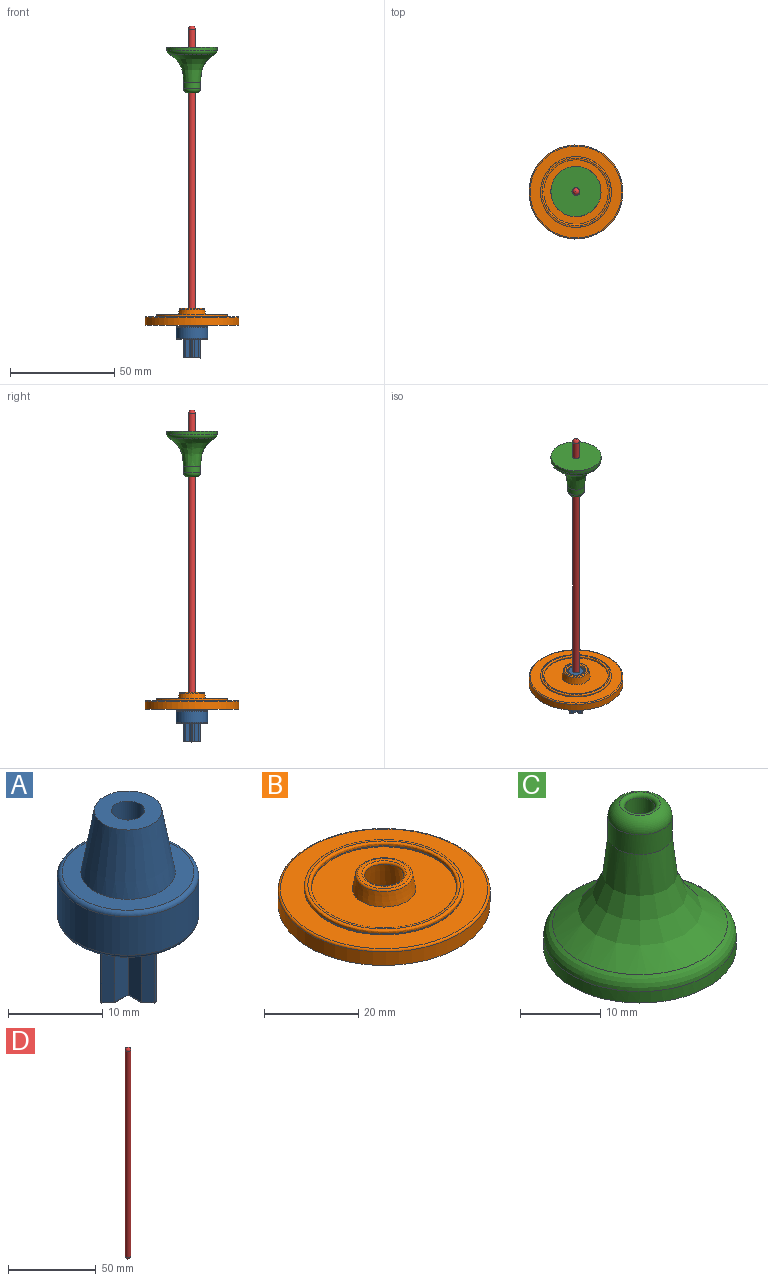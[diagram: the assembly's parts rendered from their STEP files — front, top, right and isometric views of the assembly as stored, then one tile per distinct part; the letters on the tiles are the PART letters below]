
ASSEMBLY  parts=4 mates=4
PART A: 51 faces, bbox 16.2x16.2x23 mm
  f0: cylinder r=7.5mm len=15mm, axis (0,0,-1), area 235.6mm2, adj f49,f50
  f1: plane 14x14mm, normal (0,0,1), area 75.4mm2, adj f44,f50
  f2: plane 14x14mm, normal (0,0,-1), area 126.7mm2, adj f3,f4,f5,f6,f7,f8,f9,f10
  f3: plane 8.8x2mm, normal (-1,0,0), area 17.6mm2, adj f2,f4,f18,f38
  f4: plane 8.8x2mm, normal (0,-1,0), area 17.6mm2, adj f2,f3,f13,f41
  f5: plane 8.8x2mm, normal (0,1,0), area 17.6mm2, adj f2,f6,f12,f37
  f6: plane 8.8x2mm, normal (-1,0,0), area 17.6mm2, adj f2,f5,f15,f35
  f7: plane 8.8x2mm, normal (1,0,0), area 17.6mm2, adj f2,f8,f14,f25
  f8: plane 8.8x2mm, normal (0,1,0), area 17.6mm2, adj f2,f7,f17,f23
  f9: plane 8.8x2mm, normal (0,-1,0), area 17.6mm2, adj f2,f10,f16,f26
  f10: plane 8.8x2mm, normal (1,0,0), area 17.6mm2, adj f2,f9,f19,f29
  f11: plane 7.83x7.83mm, normal (0,0,-1), area 21.7mm2, adj f21,f23,f24,f25,f26,f27,f29,f32
  f12: plane 8.8x0.96mm, normal (-0.71,0.71,0), area 11.9mm2, adj f2,f5,f39,f40
  f13: plane 8.8x0.96mm, normal (-0.71,-0.71,0), area 11.9mm2, adj f2,f4,f40,f43
  f14: plane 8.8x0.96mm, normal (0.71,0.71,0), area 11.9mm2, adj f2,f7,f27,f28
  f15: plane 8.8x0.96mm, normal (-0.71,0.71,0), area 11.9mm2, adj f2,f6,f28,f33
  f16: plane 8.8x0.96mm, normal (0.71,-0.71,0), area 11.9mm2, adj f2,f9,f20,f24
  f17: plane 8.8x0.96mm, normal (0.71,0.71,0), area 11.9mm2, adj f2,f8,f20,f21
  f18: plane 8.8x0.96mm, normal (-0.71,-0.71,0), area 11.9mm2, adj f2,f3,f31,f36
  f19: plane 8.8x0.96mm, normal (0.71,-0.71,0), area 11.9mm2, adj f2,f10,f31,f32
  f20: cylinder r=0.2mm len=8.8mm, axis (0,0,-1), area 2.8mm2, adj f2,f16,f17,f22
  f21: cylinder r=0.2mm len=1.1mm, axis (-0.71,0.71,0), area 0.4mm2, adj f11,f17,f22,f23
  f22: sphere r=0.2mm, area 0.1mm2, adj f20,f21,f24
  f23: cylinder r=0.2mm len=2.2mm, axis (-1,0,0), area 0.6mm2, adj f8,f11,f21,f25
  f24: cylinder r=0.2mm len=1.1mm, axis (0.71,0.71,0), area 0.4mm2, adj f11,f16,f22,f26
  f25: cylinder r=0.2mm len=2.2mm, axis (0,1,0), area 0.6mm2, adj f7,f11,f23,f27
  f26: cylinder r=0.2mm len=2.2mm, axis (1,0,0), area 0.6mm2, adj f9,f11,f24,f29
  f27: cylinder r=0.2mm len=1.1mm, axis (-0.71,0.71,0), area 0.4mm2, adj f11,f14,f25,f30
  f28: cylinder r=0.2mm len=8.8mm, axis (0,0,-1), area 2.8mm2, adj f2,f14,f15,f30
  f29: cylinder r=0.2mm len=2.2mm, axis (0,1,0), area 0.6mm2, adj f10,f11,f26,f32
  f30: sphere r=0.2mm, area 0.1mm2, adj f27,f28,f33
  f31: cylinder r=0.2mm len=8.8mm, axis (0,0,-1), area 2.8mm2, adj f2,f18,f19,f34
  f32: cylinder r=0.2mm len=1.1mm, axis (0.71,0.71,0), area 0.4mm2, adj f11,f19,f29,f34
  f33: cylinder r=0.2mm len=1.1mm, axis (-0.71,-0.71,0), area 0.4mm2, adj f11,f15,f30,f35
  f34: sphere r=0.2mm, area 0.1mm2, adj f31,f32,f36
  f35: cylinder r=0.2mm len=2.2mm, axis (0,-1,0), area 0.6mm2, adj f6,f11,f33,f37
  f36: cylinder r=0.2mm len=1.1mm, axis (0.71,-0.71,0), area 0.4mm2, adj f11,f18,f34,f38
  f37: cylinder r=0.2mm len=2.2mm, axis (-1,0,0), area 0.6mm2, adj f5,f11,f35,f39
  f38: cylinder r=0.2mm len=2.2mm, axis (0,-1,0), area 0.6mm2, adj f3,f11,f36,f41
  f39: cylinder r=0.2mm len=1.1mm, axis (-0.71,-0.71,0), area 0.4mm2, adj f11,f12,f37,f42
  f40: cylinder r=0.2mm len=8.8mm, axis (0,0,-1), area 2.8mm2, adj f2,f12,f13,f42
  f41: cylinder r=0.2mm len=2.2mm, axis (1,0,0), area 0.6mm2, adj f4,f11,f38,f43
  f42: sphere r=0.2mm, area 0.1mm2, adj f39,f40,f43
  f43: cylinder r=0.2mm len=1.1mm, axis (0.71,-0.71,0), area 0.4mm2, adj f11,f13,f41,f42
  f44: cone r=5mm half-angle=10deg, axis (0,0,-1), area 219.2mm2, adj f1,f45
  f45: plane 7.18x7.18mm, normal (0,0,1), area 30.9mm2, adj f44,f46
  f46: cylinder r=1.75mm len=8.9mm, axis (0,0,1), area 97.9mm2, adj f45,f48
  f47: plane 0.3x0.3mm, normal (0,0,1), area 0.1mm2, adj f48
  f48: torus R=0.15mm, axis (0,0,1), area 18.5mm2, adj f46,f47
  f49: torus R=7mm, axis (0,0,1), area 36.1mm2, adj f0,f2
  f50: torus R=7mm, axis (0,0,1), area 36.1mm2, adj f0,f1
PART B: 14 faces, bbox 48.7x48.7x8 mm
  f0: plane 30.85x30.85mm, normal (0,0,1), area 606.2mm2, adj f4,f7
  f1: cylinder r=22.5mm len=45mm, axis (0,0,-1), area 494.8mm2, adj f3,f11
  f2: plane 44x44mm, normal (0,0,1), area 620.6mm2, adj f8,f11
  f3: plane 45x45mm, normal (0,0,-1), area 1495.4mm2, adj f1,f6
  f4: cone r=6mm half-angle=10deg, axis (0,0,-1), area 146.2mm2, adj f0,f13
  f5: plane 11.16x11.16mm, normal (0,0,1), area 28.9mm2, adj f12,f13
  f6: cone r=5.5mm half-angle=10deg, axis (0,0,-1), area 229.2mm2, adj f3,f12
  f7: cylinder r=15.42mm len=30.85mm, axis (0,0,-1), area 24.2mm2, adj f0,f10
  f8: cylinder r=16.93mm len=33.85mm, axis (0,0,-1), area 26.6mm2, adj f2,f9
  f9: bspline ~34.73x34.73mm, area 139mm2, adj f8,f10
  f10: bspline ~33.19x33.19mm, area 130.2mm2, adj f7,f9
  f11: torus R=22mm, axis (0,0,1), area 110.1mm2, adj f1,f2
  f12: torus R=4.69mm, axis (0,0,1), area 23.8mm2, adj f5,f6
  f13: torus R=5.58mm, axis (0,0,1), area 25.8mm2, adj f4,f5
PART C: 8 faces, bbox 39x39x22 mm
  f0: cylinder r=12mm len=24mm, axis (0,0,-1), area 131.3mm2, adj f1,f4
  f1: plane 24x24mm, normal (0,0,-1), area 441mm2, adj f0,f6
  f2: cylinder r=4mm len=8mm, axis (0,0,-1), area 75.4mm2, adj f3,f5
  f3: bspline ~38.99x38.99mm, area 615.6mm2, adj f2,f4
  f4: bspline ~24.01x24mm, area 162.6mm2, adj f0,f3
  f5: torus R=2mm, axis (0,0,1), area 56.9mm2, adj f2,f7
  f6: cylinder r=1.9mm len=21.45mm, axis (0,0,1), area 256mm2, adj f1,f7
  f7: torus R=2.4mm, axis (0,0,-1), area 12.4mm2, adj f5,f6
PART D: 3 faces, bbox 3.2x3.2x147.5 mm
  f0: cylinder r=1.6mm len=144.3mm, axis (0,0,-1), area 1450.7mm2, adj f1,f2
  f1: sphere r=1.6mm, area 16.1mm2, adj f0
  f2: sphere r=1.6mm, area 16.1mm2, adj f0
PLACE A rot(axis=(0.15,0.78,0.6),0deg) t=(-10.92,0.52,-29.94)mm
PLACE B rot(axis=(0.15,0.78,0.6),0deg) t=(-10.92,0.52,-23.23)mm
PLACE C rot(axis=(0,-1,0),180deg) t=(-10.92,0.52,109.86)mm
PLACE D rot(axis=(0.15,0.78,0.6),0deg) t=(-10.92,0.52,-27.57)mm
MATE fastened A.f46 <-> D.f0  axis (0,0,1) through (-10.92,0.52,-25.97)mm
MATE slider A.f46 <-> D.f0  axis (0,0,1) through (-10.92,0.52,-15.94)mm
MATE slider B.f6 <-> A.f44  axis (0,0,-1) through (-10.92,0.52,-15.82)mm
MATE cylindrical D.f0 <-> C.f6  axis (0,0,-1) through (-10.92,0.52,46.18)mm
